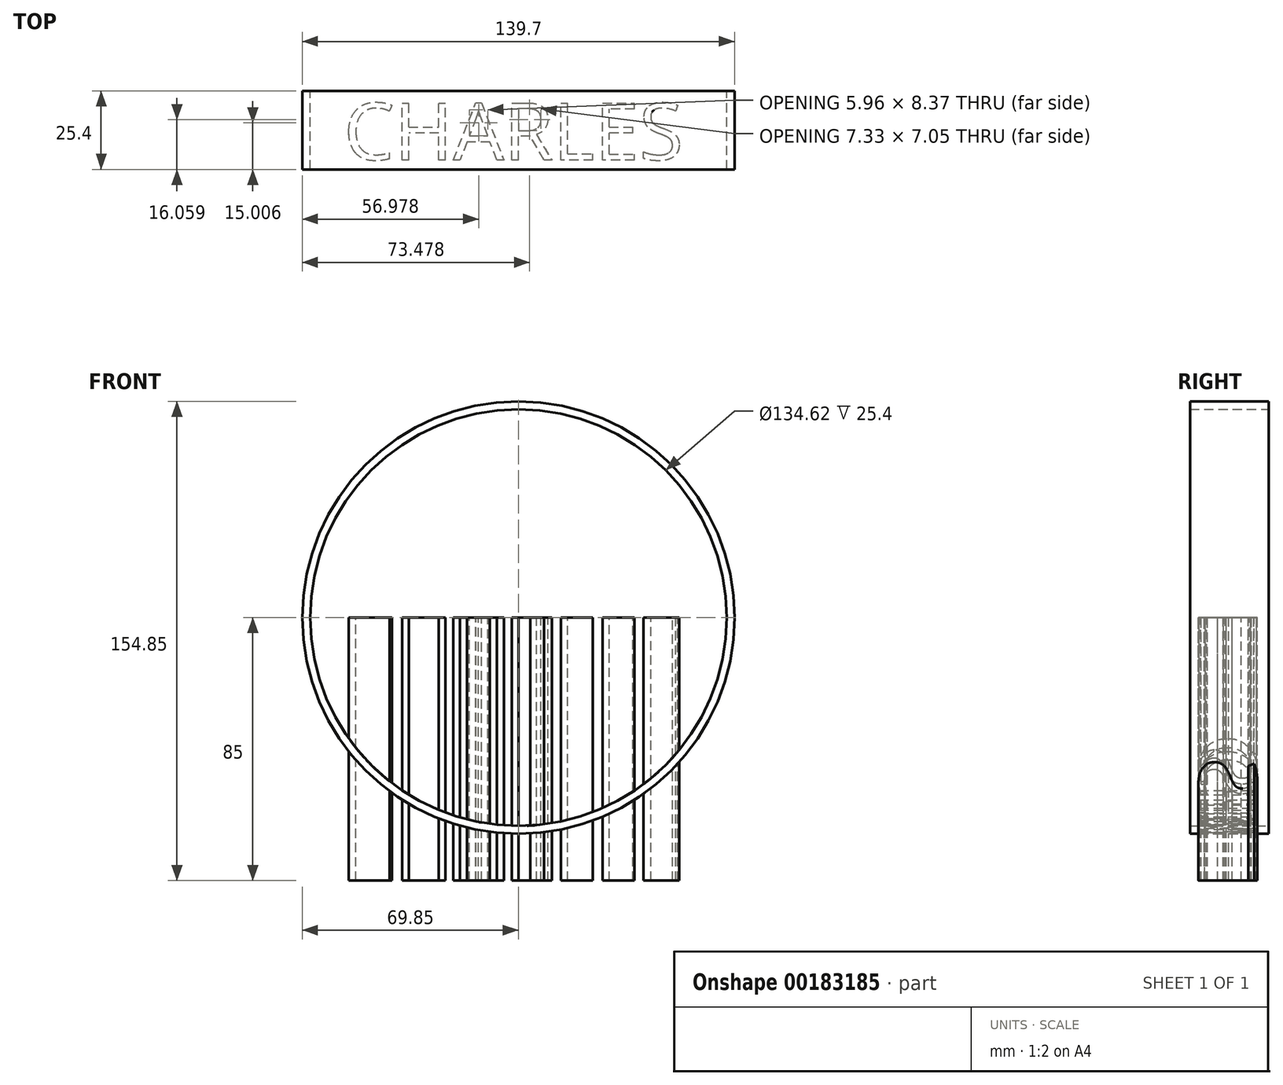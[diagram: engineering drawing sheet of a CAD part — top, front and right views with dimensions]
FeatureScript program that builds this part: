
annotation { "Feature Type Name" : "Feature", "Feature Type Description" : "" }
export const myFeature = defineFeature(function(context is Context, id is Id, definition is map)
    precondition{}
    {
        {
            var Q0;
            Q0=qCreatedBy(makeId("Front.planeOp"),FACE);
            var sketch = newSketch(context, id + "F0", { "sketchPlane" : qUnion([Q0])});
            skCircle(sketch, "E0", {"center": v(0, 0) * mm, "radius": 69.85 * mm});
            skSolve(sketch);
        }
        {
            var Q0;
            Q0=makeQuery(id+"F0.imprint","IMPRINT",FACE,{"disambiguationData":[TD([[makeQuery(id+"F0.imprint","IMPRINT",EDGE,{"derivedFrom":sQuery(id+"F0.wireOp",EDGE,"E0")}),1.0]])]});
            var sketch = newSketch(context, id + "F1", { "sketchPlane" : qUnion([Q0])});
            skCircle(sketch, "E1", {"center": v(0, 0) * mm, "radius": 55.92 * mm});
            skSolve(sketch);
        }
        {
            var Q0;
            Q0=makeQuery(id+"F0.imprint","IMPRINT",FACE,{"disambiguationData":[TD([[makeQuery(id+"F0.imprint","IMPRINT",EDGE,{"derivedFrom":sQuery(id+"F0.wireOp",EDGE,"E0")}),1.0]])]});
            extrude(context, id + "F2", {"entities" : qUnion([Q0]), "depth" : 25.4 * mm});
        }
        {
            var Q0;
            Q0=makeQuery(id+"F1.imprint","IMPRINT",FACE,{"disambiguationData":[TD([[makeQuery(id+"F1.imprint","IMPRINT",EDGE,{"derivedFrom":sQuery(id+"F1.wireOp",EDGE,"E1")}),1.0]])]});
            extrude(context, id + "F3", {"entities" : qUnion([Q0]), "operationType" : NewBodyOperationType.ADD, "depth" : 2.54 * mm});
        }
        {
            var Q0;
            Q0=makeQuery(id+"F2.opExtrude","CAP_FACE",FACE,{"disambiguationData":[OSD([sQuery(id+"F0.wireOp",EDGE,"E0")])],"isStart":false});
            var Q1;
            Q1=makeQuery(id+"F2.opExtrude","CAP_FACE",FACE,{"disambiguationData":[OSD([sQuery(id+"F0.wireOp",EDGE,"E0")])],"isStart":true});
            shell(context, id + "F4", {"entities" : qUnion([Q0, Q1]), "thickness" : 2.54 * mm});
        }
        {
            var Q0;
            Q0=qCreatedBy(makeId("Top.planeOp"),FACE);
            var sketch = newSketch(context, id + "F5", { "sketchPlane" : qUnion([Q0])});
            skText(sketch, "E2", { "text": "CHARLES", "fontName": "OpenSans-Regular.ttf"});
            const initialGuessF5  = {"E2": [-0.05639, -0.02237, 1, 0, 0.01859]};
            skSetInitialGuess(sketch, initialGuessF5);
            skSolve(sketch);
        }
        {
            var Q0;
            Q0 = qSketchRegion(id + "F5", true);
            extrude(context, id + "F6", {"entities" : qUnion([Q0]), "operationType" : NewBodyOperationType.ADD, "oppositeDirection" : true, "depth" : 85 * mm});
        }
    });
